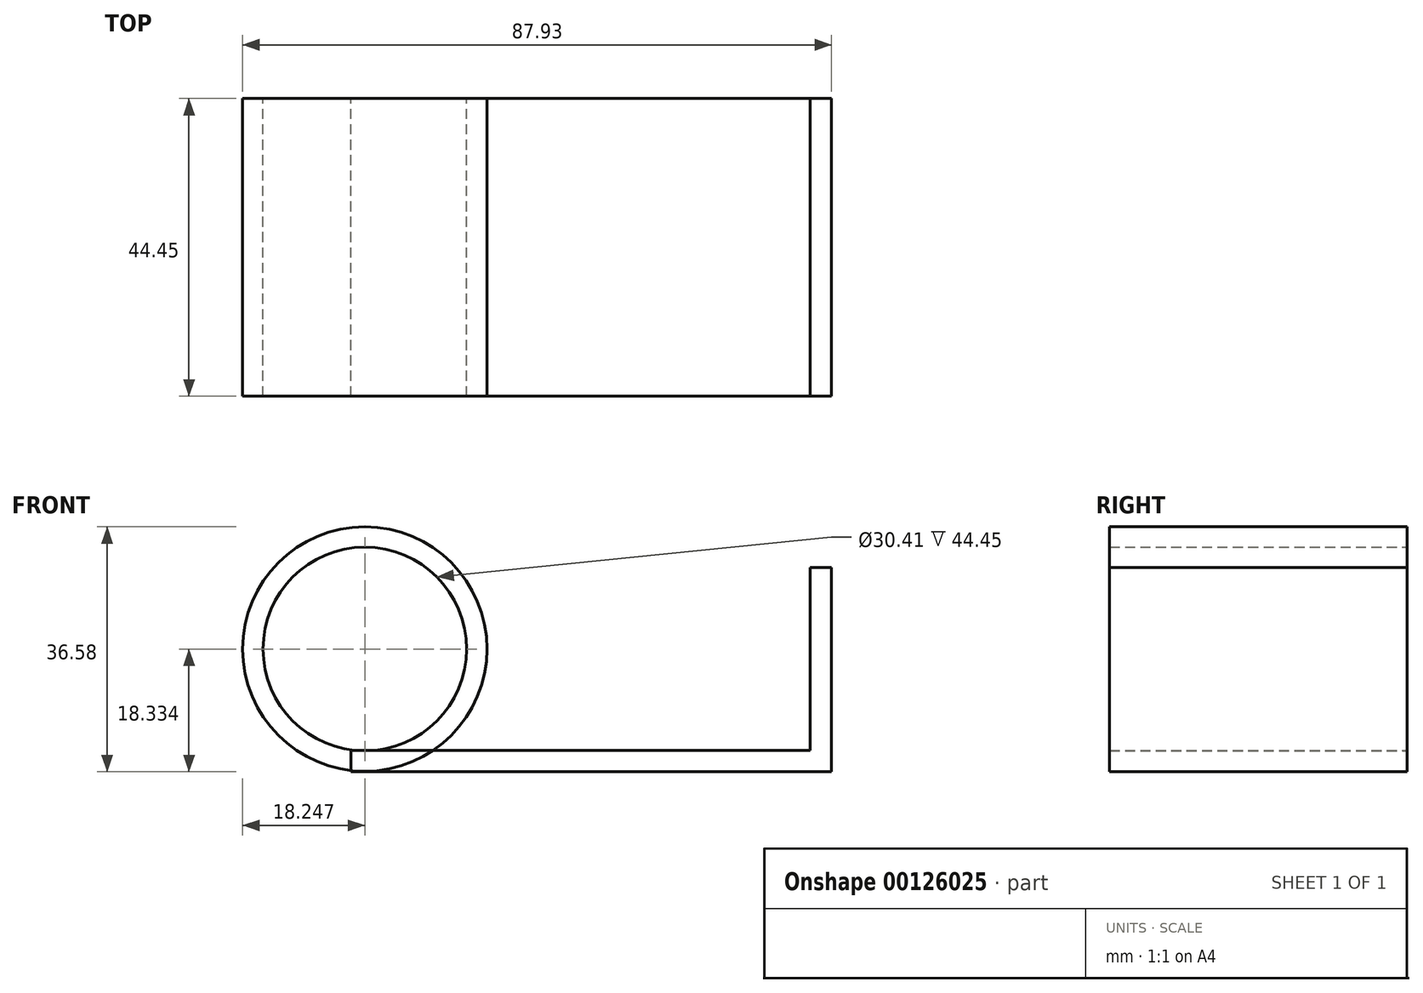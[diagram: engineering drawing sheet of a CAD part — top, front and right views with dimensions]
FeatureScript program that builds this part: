
annotation { "Feature Type Name" : "Feature", "Feature Type Description" : "" }
export const myFeature = defineFeature(function(context is Context, id is Id, definition is map)
    precondition{}
    {
        {
            var Q0;
            Q0=qCreatedBy(makeId("Front.planeOp"),FACE);
            var sketch = newSketch(context, id + "F0", { "sketchPlane" : qUnion([Q0])});
            skLineSegment(sketch, "E0.bottom", {"start": v(-43.58, 0) * mm, "end": v(25, 0) * mm});
            skLineSegment(sketch, "E0.top", {"start": v(-43.58, -3.18) * mm, "end": v(25, -3.18) * mm});
            skLineSegment(sketch, "E0.left", {"start": v(-43.58, 0) * mm, "end": v(-43.58, -3.18) * mm});
            skLineSegment(sketch, "E0.right", {"start": v(25, 0) * mm, "end": v(25, -3.18) * mm});
            skArc(sketch, "E1", {"start": v(-40.2, 30.28) * mm, "mid": v(-56.68, 16.79) * mm, "end": v(-43.58, 0) * mm});
            skArc(sketch, "E2.0", {"start": v(-39.93, 33.45) * mm, "mid": v(-59.84, 17.14) * mm, "end": v(-44, -3.15) * mm});
            skLineSegment(sketch, "E3", {"start": v(-39.93, 33.45) * mm, "end": v(-40.2, 30.28) * mm});
            skLineSegment(sketch, "E4.bottom", {"start": v(25, -3.18) * mm, "end": v(28.18, -3.18) * mm});
            skLineSegment(sketch, "E4.top", {"start": v(25, 27.3) * mm, "end": v(28.18, 27.3) * mm});
            skLineSegment(sketch, "E4.left", {"start": v(25, -3.18) * mm, "end": v(25, 27.3) * mm});
            skLineSegment(sketch, "E4.right", {"start": v(28.18, -3.18) * mm, "end": v(28.18, 27.3) * mm});
            skSolve(sketch);
        }
        {
            var Q0;
            Q0=qCreatedBy(makeId("Front.planeOp"),FACE);
            var sketch = newSketch(context, id + "F1", { "sketchPlane" : qUnion([Q0])});
            skCircle(sketch, "E5", {"center": v(-41.5, 15.15) * mm, "radius": 18.25 * mm});
            skCircle(sketch, "E6", {"center": v(-41.5, 15.15) * mm, "radius": 15.2 * mm});
            skSolve(sketch);
        }
        {
            var Q0;
            Q0 = qSketchRegion(id + "F1", true);
            var Q1;
            {var subQ0=sQuery(id+"F0.wireOp",EDGE,"E0.bottom");Q1=makeQuery(id+"F0.imprint","IMPRINT",FACE,{"disambiguationData":[TD([[makeQuery(id+"F0.imprint","IMPRINT",EDGE,{"derivedFrom":subQ0}),-1.0]])]});}
            var Q2;
            {var subQ3=sQuery(id+"F0.wireOp",EDGE,"E4.bottom");Q2=makeQuery(id+"F0.imprint","IMPRINT",FACE,{"disambiguationData":[TD([[makeQuery(id+"F0.imprint","IMPRINT",EDGE,{"derivedFrom":subQ3}),1.0]])]});}
            extrude(context, id + "F2", {"entities" : qUnion([Q0, Q1, Q2]), "depth" : 44.45 * mm});
        }
    });
